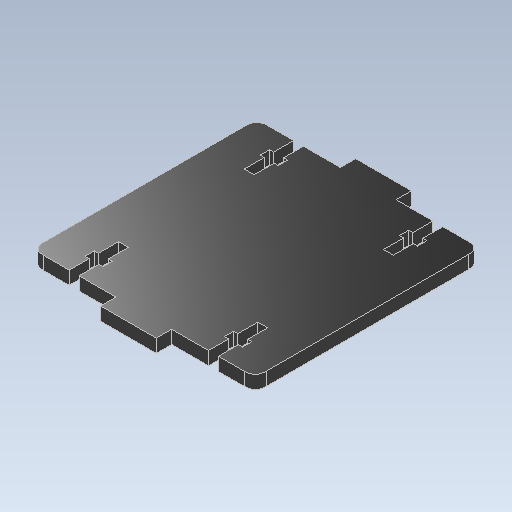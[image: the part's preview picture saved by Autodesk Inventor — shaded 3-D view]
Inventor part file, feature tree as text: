
AUTODESK INVENTOR PART (.ipt)
format: ipt  version: 2025 (Build 290162000, 162)  size: 215,552 bytes
history: native  units: mm
features: sketch x4, extrude x3, mirror x2, plane x1, fillet x1, hole x1, pattern_linear x1, projected_geometry x1
ambient origin geometry x8: Origin, YZ Plane, XZ Plane, XY Plane, X Axis, Y Axis, Z Axis, Center Point
bodies: Solid1 (feature_tree)
feature tree (14):
  extrude  "Extrusion1"  Depth=6.0mm
  plane  "Work Plane1"
  extrude  "Extrusion2"  Depth=6.0mm
  mirror  "Mirror1"
  extrude  "Extrusion3"  Depth=102.3mm
  fillet  "Fillet1"  Radius=7.0mm
  mirror  "Mirror2"
  hole  "Hole1"  [1 undecoded]
  pattern_linear  "Rectangular Pattern1"  Spacing1=0.0mm  [1 undecoded]
  sketch  "Sketch1"  dims[d1=6.0mm d2=0.0mm d3=6.7mm]
  sketch  "Sketch2"  dims[d4=4.25mm d5=6.0mm d6=4.0mm d7=2.0mm d8=90.0deg d9=8.0mm d10=20.594885mm d11=80.0mm d13=12.7mm d14=80.0mm d16=12.7mm]
  sketch  "Sketch3"  dims[d17=5.0mm d19=102.3mm d20=7.0mm]
  projected_geometry  "Projected Loop1"
  sketch  "Sketch4"  dims[d22=0.0mm d23=0.0mm d25=4.25mm d26=8.25mm d28=4.4958mm d29=0.0mm d30=0.0mm d31=25.4mm d32=22.5mm d39=101.6mm d40=6.35mm]
note: 2 required parameter values undecoded (feature->parameter linkage not recoverable at this tier; creation-order binding heuristic only, values carry confidence <= 0.55)
